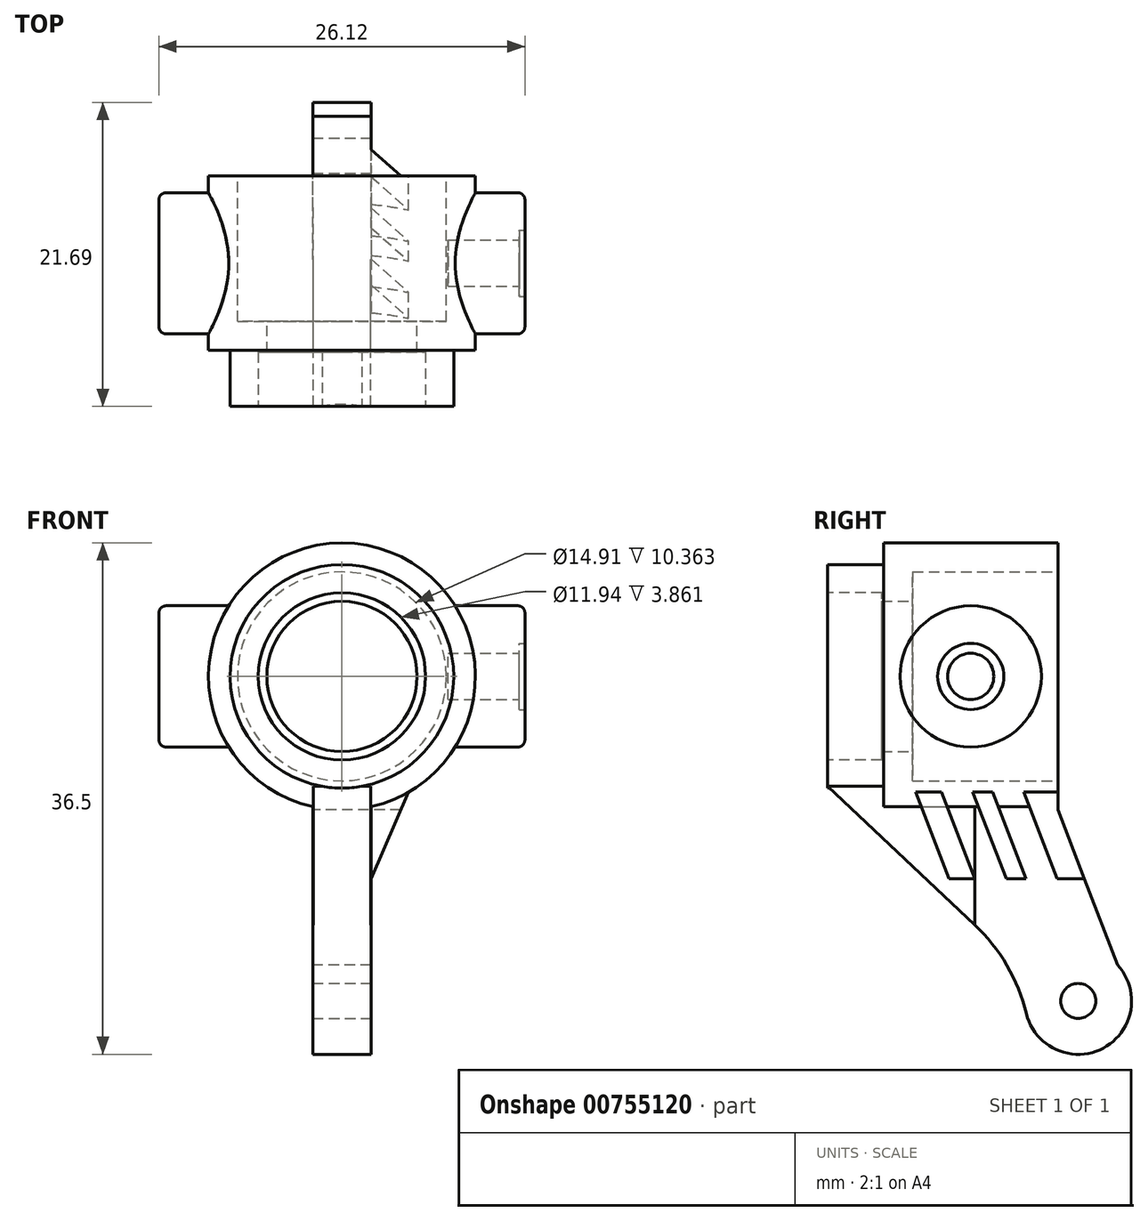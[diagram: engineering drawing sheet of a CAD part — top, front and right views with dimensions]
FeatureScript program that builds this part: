
annotation { "Feature Type Name" : "Feature", "Feature Type Description" : "" }
export const myFeature = defineFeature(function(context is Context, id is Id, definition is map)
    precondition{}
    {
        {
            var Q0;
            Q0=qCreatedBy(makeId("Front.planeOp"),FACE);
            var sketch = newSketch(context, id + "F0", { "sketchPlane" : qUnion([Q0])});
            skCircle(sketch, "E0", {"center": v(0, 0) * mm, "radius": 5.36 * mm});
            skCircle(sketch, "E1", {"center": v(0, 0) * mm, "radius": 9.53 * mm});
            skSolve(sketch);
        }
        {
            var Q0;
            Q0=makeQuery(id+"F0.imprint","IMPRINT",FACE,{"disambiguationData":[TD([[makeQuery(id+"F0.imprint","IMPRINT",EDGE,{"derivedFrom":sQuery(id+"F0.wireOp",EDGE,"E0")}),-1.0]])]});
            extrude(context, id + "F1", {"entities" : qUnion([Q0]), "depth" : 16.43 * mm, "offsetDistance" : 25.4 * mm});
        }
        {
            var Q0;
            Q0=makeQuery(id+"F1.opExtrude","CAP_FACE",FACE,{"disambiguationData":[OSD([sQuery(id+"F0.wireOp",EDGE,"E0"),sQuery(id+"F0.wireOp",EDGE,"E1")])],"isStart":true});
            var sketch = newSketch(context, id + "F2", { "sketchPlane" : qUnion([Q0])});
            skCircle(sketch, "E2", {"center": v(0, 0) * mm, "radius": 7.45 * mm});
            skSolve(sketch);
        }
        {
            var Q0;
            Q0=makeQuery(id+"F2.imprint","IMPRINT",FACE,{"disambiguationData":[TD([[makeQuery(id+"F2.imprint","IMPRINT",EDGE,{"derivedFrom":sQuery(id+"F2.wireOp",EDGE,"E2")}),1.0]])]});
            extrude(context, id + "F3", {"entities" : qUnion([Q0]), "operationType" : NewBodyOperationType.REMOVE, "oppositeDirection" : true, "depth" : 10.36 * mm, "offsetDistance" : 25.4 * mm});
        }
        {
            var Q0;
            Q0=makeQuery(id+"F1.opExtrude","CAP_FACE",FACE,{"disambiguationData":[OSD([sQuery(id+"F0.wireOp",EDGE,"E0"),sQuery(id+"F0.wireOp",EDGE,"E1")])],"isStart":false});
            var sketch = newSketch(context, id + "F4", { "sketchPlane" : qUnion([Q0])});
            skCircle(sketch, "E3", {"center": v(0, 0) * mm, "radius": 5.97 * mm});
            skSolve(sketch);
        }
        {
            var Q0;
            Q0 = qSketchRegion(id + "F4", true);
            extrude(context, id + "F5", {"entities" : qUnion([Q0]), "operationType" : NewBodyOperationType.REMOVE, "oppositeDirection" : true, "depth" : 3.86 * mm, "offsetDistance" : 25.4 * mm});
        }
        {
            var Q0;
            Q0=makeQuery(id+"F1.opExtrude","CAP_FACE",FACE,{"disambiguationData":[OSD([sQuery(id+"F0.wireOp",EDGE,"E0"),sQuery(id+"F0.wireOp",EDGE,"E1")])],"isStart":false});
            var sketch = newSketch(context, id + "F6", { "sketchPlane" : qUnion([Q0])});
            skCircle(sketch, "E4", {"center": v(0, 0) * mm, "radius": 7.98 * mm});
            skCircle(sketch, "E5.0", {"center": v(0, 0) * mm, "radius": 9.53 * mm});
            skSolve(sketch);
        }
        {
            var Q0;
            Q0 = qSketchRegion(id + "F6", true);
            extrude(context, id + "F7", {"entities" : qUnion([Q0]), "operationType" : NewBodyOperationType.REMOVE, "oppositeDirection" : true, "depth" : 4 * mm, "offsetDistance" : 25.4 * mm});
        }
        {
            var Q0;
            Q0=qCreatedBy(makeId("Right.planeOp"),FACE);
            var sketch = newSketch(context, id + "F8", { "sketchPlane" : qUnion([Q0])});
            skCircle(sketch, "E6", {"center": v(-6.22, 0) * mm, "radius": 5.04 * mm});
            skSolve(sketch);
        }
        {
            var Q0;
            Q0 = qSketchRegion(id + "F8", true);
            extrude(context, id + "F9", {"entities" : qUnion([Q0]), "operationType" : NewBodyOperationType.ADD, "endBound" : BoundingType.SYMMETRIC, "depth" : 26.1 * mm, "offsetDistance" : 25.4 * mm});
        }
        {
            var Q0;
            Q0=makeQuery(id+"F9.opExtrude","CAP_FACE",FACE,{"disambiguationData":[OSD([sQuery(id+"F8.wireOp",EDGE,"E6")])],"isStart":false});
            var sketch = newSketch(context, id + "F10", { "sketchPlane" : qUnion([Q0])});
            skPoint(sketch, "E7", {"position": v(-6.22, 0) * mm});
            skSolve(sketch);
        }
        {
            var Q0;
            Q0=qCreatedBy(makeId("Top.planeOp"),FACE);
            var sketch = newSketch(context, id + "F11", { "sketchPlane" : qUnion([Q0])});
            skLineSegment(sketch, "E8.0", {"start": v(-7.45, 0) * mm, "end": v(0, 0) * mm});
            skLineSegment(sketch, "E9", {"start": v(-7.45, -10.36) * mm, "end": v(-7.45, 0) * mm});
            skLineSegment(sketch, "E10", {"start": v(-5.97, -16.43) * mm, "end": v(-5.97, -12.57) * mm});
            skLineSegment(sketch, "E11.0", {"start": v(-4.52, -10.36) * mm, "end": v(0, -10.36) * mm, "construction": true});
            skLineSegment(sketch, "E12.0", {"start": v(0, -12.57) * mm, "end": v(-5.36, -12.57) * mm, "construction": true});
            skLineSegment(sketch, "E13", {"start": v(-5.36, -12.62) * mm, "end": v(-5.36, -10.37) * mm});
            skLineSegment(sketch, "E14", {"start": v(-5.97, -12.57) * mm, "end": v(-5.36, -12.57) * mm});
            skLineSegment(sketch, "E15", {"start": v(0, 0) * mm, "end": v(0, -16.43) * mm});
            skPoint(sketch, "E16.orphan", {"position": v(5.36, -12.57) * mm});
            skPoint(sketch, "E17.orphan", {"position": v(4.52, -10.36) * mm});
            skPoint(sketch, "E18.0.start.orphan", {"position": v(7.98, -16.43) * mm});
            skLineSegment(sketch, "E19.trimOffspring", {"start": v(0, 0) * mm, "end": v(-7.45, 0) * mm});
            skPoint(sketch, "E20.0.end.orphan", {"position": v(7.45, 0) * mm});
            skPoint(sketch, "E20.0.start.orphan", {"position": v(9.53, 0) * mm});
            skLineSegment(sketch, "E21.0", {"start": v(6.88, -10.36) * mm, "end": v(4.52, -10.36) * mm, "construction": true});
            skPoint(sketch, "E22.orphan", {"position": v(-6.88, -10.36) * mm});
            skLineSegment(sketch, "E23", {"start": v(-5.36, -10.37) * mm, "end": v(-5.36, -10.36) * mm});
            skLineSegment(sketch, "E24.trimOffspring", {"start": v(-5.36, -10.36) * mm, "end": v(-7.45, -10.36) * mm});
            skPoint(sketch, "E25.orphan", {"position": v(-7.98, -16.43) * mm});
            skLineSegment(sketch, "E26.0", {"start": v(0, -16.43) * mm, "end": v(-5.97, -16.43) * mm});
            skPoint(sketch, "E27.orphan", {"position": v(-9.53, 0) * mm});
            skSolve(sketch);
        }
        {
            var Q0;
            Q0 = qSketchRegion(id + "F11", true);
            var Q1;
            Q1=sQuery(id+"F11.wireOp",EDGE,"E15");
            revolve(context, id + "F12", {"operationType" : NewBodyOperationType.REMOVE, "surfaceOperationType" : NewSurfaceOperationType.NEW, "entities" : qUnion([Q0]), "axis" : qUnion([Q1]), "revolveType" : RevolveType.FULL, "oppositeDirection" : true});
        }
        {
            var Q0;
            Q0=qCreatedBy(makeId("Right.planeOp"),FACE);
            var sketch = newSketch(context, id + "F13", { "sketchPlane" : qUnion([Q0])});
            skLineSegment(sketch, "E28", {"start": v(-16.43, 7.98) * mm, "end": v(-12.45, 7.98) * mm});
            skLineSegment(sketch, "E29", {"start": v(-16.43, -7.85) * mm, "end": v(-5.94, -17.73) * mm});
            skLineSegment(sketch, "E30", {"start": v(-5.94, -17.73) * mm, "end": v(-5.94, -7.85) * mm});
            skLineSegment(sketch, "E31", {"start": v(-16.43, -7.85) * mm, "end": v(-5.94, -7.85) * mm});
            skSolve(sketch);
        }
        {
            var Q0;
            Q0 = qSketchRegion(id + "F13", true);
            extrude(context, id + "F14", {"entities" : qUnion([Q0]), "operationType" : NewBodyOperationType.ADD, "endBound" : BoundingType.SYMMETRIC, "depth" : 4.11 * mm, "offsetDistance" : 25.4 * mm});
        }
        {
            var Q0;
            Q0=qCreatedBy(makeId("Right.planeOp"),FACE);
            var sketch = newSketch(context, id + "F15", { "sketchPlane" : qUnion([Q0])});
            skArc(sketch, "E32", {"start": v(-2.25, -24.07) * mm, "mid": v(3.23, -26.53) * mm, "end": v(4.27, -20.6) * mm});
            skArc(sketch, "E33", {"start": v(-2.25, -24.07) * mm, "mid": v(-3.64, -20.63) * mm, "end": v(-5.94, -17.73) * mm});
            skPoint(sketch, "E34.0", {"position": v(-5.94, -17.73) * mm});
            skLineSegment(sketch, "E35.0", {"start": v(-16.43, -7.85) * mm, "end": v(-5.94, -17.73) * mm, "construction": true});
            skLineSegment(sketch, "E36", {"start": v(0, -9.52) * mm, "end": v(4.27, -20.6) * mm});
            skPoint(sketch, "E37.orphan", {"position": v(5.26, -23.16) * mm});
            skLineSegment(sketch, "E38.0", {"start": v(-5.94, -17.73) * mm, "end": v(-5.94, -9.53) * mm});
            skLineSegment(sketch, "E39", {"start": v(0, -9.53) * mm, "end": v(-5.94, -9.53) * mm, "construction": true});
            skLineSegment(sketch, "E40", {"start": v(-12.45, 9.53) * mm, "end": v(0, 9.53) * mm, "construction": true});
            skPoint(sketch, "E41.orphan", {"position": v(-5.94, -9.3) * mm});
            skLineSegment(sketch, "E42.0", {"start": v(0, -8.26) * mm, "end": v(-5.94, -8.26) * mm});
            skLineSegment(sketch, "E43", {"start": v(-5.94, -8.26) * mm, "end": v(-5.94, -9.53) * mm});
            skPoint(sketch, "E44.orphan", {"position": v(0, 9.53) * mm});
            skLineSegment(sketch, "E45.0.0", {"start": v(0, -8.26) * mm, "end": v(0, -9.53) * mm});
            skLineSegment(sketch, "E46", {"start": v(8.37, -26.97) * mm, "end": v(20.08, -26.97) * mm, "construction": true});
            skSolve(sketch);
        }
        {
            var Q0;
            Q0=makeQuery(id+"F15.imprint","IMPRINT",FACE,{"disambiguationData":[TD([[makeQuery(id+"F15.imprint","IMPRINT",EDGE,{"derivedFrom":sQuery(id+"F15.wireOp",EDGE,"E32")}),1.0]])]});
            extrude(context, id + "F16", {"entities" : qUnion([Q0]), "operationType" : NewBodyOperationType.ADD, "endBound" : BoundingType.SYMMETRIC, "depth" : 4.17 * mm, "offsetDistance" : 25.4 * mm});
        }
        {
            var Q0;
            Q0=makeQuery(id+"F16.opExtrude","CAP_FACE",FACE,{"disambiguationData":[OSD([sQuery(id+"F15.wireOp",EDGE,"E32"),sQuery(id+"F15.wireOp",EDGE,"E33"),sQuery(id+"F15.wireOp",EDGE,"E36"),sQuery(id+"F15.wireOp",EDGE,"E38.0"),sQuery(id+"F15.wireOp",EDGE,"E42.0"),sQuery(id+"F15.wireOp",EDGE,"E43"),sQuery(id+"F15.wireOp",EDGE,"E45.0.0")])],"isStart":false});
            var sketch = newSketch(context, id + "F17", { "sketchPlane" : qUnion([Q0])});
            skPoint(sketch, "E47", {"position": v(1.45, -23.16) * mm});
            skSolve(sketch);
        }
        {
            var Q0;
            Q0=sQuery(id+"F17.wireOp",VERTEX,"E47");
            var Q1;
            Q1=makeQuery(id+"F1.opExtrude","SWEPT_BODY",BODY,{"disambiguationData":[OSD([sQuery(id+"F0.wireOp",EDGE,"E0"),sQuery(id+"F0.wireOp",EDGE,"E1")])]});
            hole(context, id + "F18", {"style" : HoleStyle.SIMPLE, "endStyle" : HoleEndStyle.THROUGH, "standardTappedOrClearance" : lookupTablePath({ "fit" : "Normal", "standard" : "ISO", "engagement" : "75%", "pitch" : "0.5 mm", "size" : "2.5", "type" : "Drilled" }), "standardBlindInLast" : lookupTablePath({ "fit" : "Free", "standard" : "ISO", "engagement" : "75%", "pitch" : "0.5 mm", "size" : "2.5", "type" : "Drilled" }), "holeDiameter" : 2.5 * mm, "majorDiameter" : 3 * mm, "showTappedDepth" : true, "isTappedThrough" : true, "tappedDepth" : 12.7 * mm, "tapClearance" : 3, "locations" : qUnion([Q0]), "scope" : qUnion([Q1])});
        }
        {
            var Q0;
            Q0=makeQuery(id+"F9.opExtrude","CAP_EDGE",EDGE,{"disambiguationData":[OSD([sQuery(id+"F8.wireOp",EDGE,"E6")])],"isStart":false});
            var Q1;
            Q1=makeQuery(id+"F9.opExtrude","CAP_EDGE",EDGE,{"disambiguationData":[OSD([sQuery(id+"F8.wireOp",EDGE,"E6")])],"isStart":true});
            fillet(context, id + "F19", {"entities" : qUnion([Q0, Q1]), "radius" : 0.5 * mm, "tangentPropagation" : true, "allowEdgeOverflow" : false});
        }
        {
            var Q0;
            Q0=makeQuery(id+"F9.opExtrude","CAP_FACE",FACE,{"disambiguationData":[OSD([sQuery(id+"F8.wireOp",EDGE,"E6")])],"isStart":false});
            var sketch = newSketch(context, id + "F20", { "sketchPlane" : qUnion([Q0])});
            skCircle(sketch, "E48", {"center": v(-6.22, 0) * mm, "radius": 2.36 * mm});
            skSolve(sketch);
        }
        {
            var Q0;
            Q0 = qSketchRegion(id + "F20", true);
            extrude(context, id + "F21", {"entities" : qUnion([Q0]), "operationType" : NewBodyOperationType.REMOVE, "oppositeDirection" : true, "depth" : 0.4 * mm, "offsetDistance" : 25.4 * mm});
        }
        {
            var Q0;
            Q0=makeQuery(id+"F16.opExtrude","CAP_FACE",FACE,{"disambiguationData":[OSD([sQuery(id+"F15.wireOp",EDGE,"E32"),sQuery(id+"F15.wireOp",EDGE,"E33"),sQuery(id+"F15.wireOp",EDGE,"E36"),sQuery(id+"F15.wireOp",EDGE,"E38.0"),sQuery(id+"F15.wireOp",EDGE,"E42.0"),sQuery(id+"F15.wireOp",EDGE,"E43"),sQuery(id+"F15.wireOp",EDGE,"E45.0.0")])],"isStart":false});
            var sketch = newSketch(context, id + "F22", { "sketchPlane" : qUnion([Q0])});
            skLineSegment(sketch, "E49.0", {"start": v(0, -9.52) * mm, "end": v(1.89, -14.43) * mm});
            skLineSegment(sketch, "E50", {"start": v(1.89, -14.43) * mm, "end": v(0, -14.43) * mm});
            skLineSegment(sketch, "E51.0", {"start": v(-1.94, -9.3) * mm, "end": v(0.04, -14.43) * mm});
            skPoint(sketch, "E52.orphan", {"position": v(4.27, -20.6) * mm});
            skLineSegment(sketch, "E53.0", {"start": v(-1.94, -9.3) * mm, "end": v(0, -9.3) * mm});
            skPoint(sketch, "E54.orphan", {"position": v(-5.94, -9.3) * mm});
            skLineSegment(sketch, "E55", {"start": v(0, -9.3) * mm, "end": v(0, -9.52) * mm});
            skSolve(sketch);
        }
        {
            var Q0;
            Q0=sQuery(id+"F22.wireOp",VERTEX,"E50.start");
            var Q1;
            Q1=qCreatedBy(makeId("Front.planeOp"),FACE);
            cPlane(context, id + "F23", {"entities" : qUnion([Q0, Q1]), "cplaneType" : CPlaneType.PLANE_POINT, "offset" : 25.4 * mm, "width" : 152.4 * mm, "height" : 152.4 * mm});
        }
        {
            var Q0;
            Q0=qCreatedBy(id+"F23.planeOp",FACE);
            var sketch = newSketch(context, id + "F24", { "sketchPlane" : qUnion([Q0])});
            skLineSegment(sketch, "E56", {"start": v(0, -43.17) * mm, "end": v(101.89, -43.17) * mm});
            skPoint(sketch, "E57.0", {"position": v(2.08, -14.43) * mm});
            skLineSegment(sketch, "E58", {"start": v(2.08, -14.43) * mm, "end": v(4.76, -8.25) * mm});
            skLineSegment(sketch, "E59", {"start": v(4.76, -8.25) * mm, "end": v(4.76, -8.25) * mm});
            skLineSegment(sketch, "E60.0", {"start": v(2.08, -8.25) * mm, "end": v(2.08, -14.43) * mm});
            skLineSegment(sketch, "E61", {"start": v(4.76, -8.25) * mm, "end": v(2.08, -8.25) * mm});
            skPoint(sketch, "E62.orphan", {"position": v(2.08, -9.52) * mm});
            skSolve(sketch);
        }
        {
            var Q0;
            Q0=makeQuery(id+"F24.imprint","IMPRINT",FACE,{"disambiguationData":[TD([[makeQuery(id+"F24.imprint","IMPRINT",EDGE,{"derivedFrom":sQuery(id+"F24.wireOp",EDGE,"E58")}),1.0]])]});
            extrude(context, id + "F25", {"entities" : qUnion([Q0]), "operationType" : NewBodyOperationType.ADD, "depth" : 14.33 * mm, "offsetDistance" : 25.4 * mm});
        }
        {
            var Q0;
            {var subQ2=sQuery(id+"F22.wireOp",EDGE,"E51.0");Q0=makeQuery(id+"F22.imprint","IMPRINT",FACE,{"disambiguationData":[TD([[makeQuery(id+"F22.imprint","IMPRINT",EDGE,{"derivedFrom":subQ2}),-1.0]])]});}
            var sketch = newSketch(context, id + "F26", { "sketchPlane" : qUnion([Q0])});
            skLineSegment(sketch, "E63.0", {"start": v(0, -9.52) * mm, "end": v(1.89, -14.43) * mm});
            skLineSegment(sketch, "E64.0", {"start": v(0, -8.25) * mm, "end": v(0, -9.52) * mm});
            skLineSegment(sketch, "E65.0", {"start": v(1.89, -14.43) * mm, "end": v(1.89, -8.25) * mm});
            skLineSegment(sketch, "E66.0", {"start": v(0, -8.25) * mm, "end": v(1.89, -8.25) * mm});
            skPoint(sketch, "E67.0.end.orphan", {"position": v(0, 9.53) * mm});
            skPoint(sketch, "E67.0.start.orphan", {"position": v(0, -8.25) * mm});
            skPoint(sketch, "E68.0.end.orphan", {"position": v(4.27, -20.6) * mm});
            skSolve(sketch);
        }
        {
            var Q0;
            Q0 = qSketchRegion(id + "F26", true);
            extrude(context, id + "F27", {"entities" : qUnion([Q0]), "operationType" : NewBodyOperationType.REMOVE, "endBound" : BoundingType.SYMMETRIC, "oppositeDirection" : true, "depth" : 25.4 * mm, "offsetDistance" : 25.4 * mm});
        }
        {
            var Q0;
            Q0=makeQuery(id+"F16.opExtrude","CAP_FACE",FACE,{"disambiguationData":[OSD([sQuery(id+"F15.wireOp",EDGE,"E32"),sQuery(id+"F15.wireOp",EDGE,"E33"),sQuery(id+"F15.wireOp",EDGE,"E36"),sQuery(id+"F15.wireOp",EDGE,"E38.0"),sQuery(id+"F15.wireOp",EDGE,"E42.0"),sQuery(id+"F15.wireOp",EDGE,"E43"),sQuery(id+"F15.wireOp",EDGE,"E45.0.0")])],"isStart":false});
            var sketch = newSketch(context, id + "F28", { "sketchPlane" : qUnion([Q0])});
            skLineSegment(sketch, "E69.0", {"start": v(1.89, -14.43) * mm, "end": v(0, -9.52) * mm});
            skLineSegment(sketch, "E70.0", {"start": v(-12.44, -8.25) * mm, "end": v(0, -8.25) * mm, "construction": true});
            skLineSegment(sketch, "E71.0", {"start": v(-0.04, -14.43) * mm, "end": v(-2.42, -8.25) * mm});
            skLineSegment(sketch, "E72.0", {"start": v(-2.28, -14.43) * mm, "end": v(-4.66, -8.25) * mm});
            skLineSegment(sketch, "E73.0", {"start": v(-3.7, -14.43) * mm, "end": v(-6.07, -8.25) * mm});
            skLineSegment(sketch, "E74.0", {"start": v(-5.92, -14.43) * mm, "end": v(-8.3, -8.25) * mm});
            skLineSegment(sketch, "E75.0", {"start": v(-7.77, -14.43) * mm, "end": v(-10.16, -8.25) * mm});
            skLineSegment(sketch, "E76.0", {"start": v(-5.94, -14.43) * mm, "end": v(1.89, -14.43) * mm, "construction": true});
            skLineSegment(sketch, "E77.0", {"start": v(-12.44, -14.43) * mm, "end": v(-5.94, -14.43) * mm, "construction": true});
            skLineSegment(sketch, "E78", {"start": v(-2.28, -14.43) * mm, "end": v(-0.04, -14.43) * mm});
            skLineSegment(sketch, "E79", {"start": v(-4.66, -8.25) * mm, "end": v(-2.42, -8.25) * mm});
            skLineSegment(sketch, "E80", {"start": v(-5.92, -14.43) * mm, "end": v(-3.7, -14.43) * mm});
            skLineSegment(sketch, "E81", {"start": v(-6.07, -8.25) * mm, "end": v(-8.3, -8.25) * mm});
            skLineSegment(sketch, "E82", {"start": v(-7.77, -14.43) * mm, "end": v(-12.44, -14.43) * mm});
            skLineSegment(sketch, "E83", {"start": v(-12.44, -8.25) * mm, "end": v(-12.44, -14.43) * mm});
            skLineSegment(sketch, "E84", {"start": v(-10.16, -8.25) * mm, "end": v(-12.44, -8.25) * mm});
            skSolve(sketch);
        }
        {
            var Q0;
            Q0 = qSketchRegion(id + "F28", true);
            extrude(context, id + "F29", {"entities" : qUnion([Q0]), "operationType" : NewBodyOperationType.REMOVE, "depth" : 25.4 * mm, "offsetDistance" : 25.4 * mm});
        }
        {
            var Q0;
            Q0=makeQuery(id+"F7.boolean.opBoolean","COPY",FACE,{"derivedFrom":makeQuery(id+"F7.opExtrude","CAP_FACE",FACE,{"disambiguationData":[OSD([sQuery(id+"F6.wireOp",EDGE,"E4"),sQuery(id+"F6.wireOp",EDGE,"E5.0")])],"isStart":false})});
            var sketch = newSketch(context, id + "F30", { "sketchPlane" : qUnion([Q0])});
            skLineSegment(sketch, "E85.0", {"start": v(-4.76, -8.25) * mm, "end": v(2.08, -8.25) * mm});
            skLineSegment(sketch, "E86.0", {"start": v(4.76, -8.25) * mm, "end": v(2.08, -8.25) * mm});
            skArc(sketch, "E87.converted", {"start": v(-4.76, -8.25) * mm, "mid": v(0, -9.53) * mm, "end": v(4.76, -8.25) * mm});
            skPoint(sketch, "E88.orphan", {"position": v(-2.06, -9.3) * mm});
            skPoint(sketch, "E89.orphan", {"position": v(-2.08, -8.25) * mm});
            skSolve(sketch);
        }
        {
            var Q0;
            Q0 = qSketchRegion(id + "F30", true);
            var Q1;
            Q1=makeQuery(id+"F27.boolean.opBoolean","MERGE",FACE,{"derivedFrom":[makeQuery(id+"F16.boolean.opBoolean","MERGE",FACE,{"derivedFrom":[makeQuery(id+"F1.opExtrude","CAP_FACE",FACE,{"disambiguationData":[OSD([sQuery(id+"F0.wireOp",EDGE,"E0"),sQuery(id+"F0.wireOp",EDGE,"E1")])],"isStart":true}),makeQuery(id+"F16.opExtrude","SWEPT_FACE",FACE,{"disambiguationData":[OSD([sQuery(id+"F15.wireOp",EDGE,"E45.0.0")])]})]}),makeQuery(id+"F27.opExtrude","SWEPT_FACE",FACE,{"disambiguationData":[OSD([sQuery(id+"F26.wireOp",EDGE,"E64.0")])]})]});
            extrude(context, id + "F31", {"entities" : qUnion([Q0]), "operationType" : NewBodyOperationType.ADD, "endBound" : BoundingType.UP_TO_SURFACE, "oppositeDirection" : true, "depth" : 25.4 * mm, "endBoundEntityFace" : qUnion([Q1]), "offsetDistance" : 25.4 * mm});
        }
        {
            var Q0;
            Q0=makeQuery(id+"F10.imprint","IMPRINT",FACE,{"disambiguationData":[TD([[makeQuery(id+"F10.imprint","IMPRINT",EDGE,{"derivedFrom":makeQuery(id+"F9.opExtrude","CAP_EDGE",EDGE,{"disambiguationData":[OSD([sQuery(id+"F8.wireOp",EDGE,"E6")])],"isStart":false})}),1.0]])]});
            var sketch = newSketch(context, id + "F32", { "sketchPlane" : qUnion([Q0])});
            skCircle(sketch, "E90", {"center": v(-6.22, 0) * mm, "radius": 1.65 * mm});
            skSolve(sketch);
        }
        {
            var Q0;
            Q0 = qSketchRegion(id + "F32", true);
            extrude(context, id + "F33", {"entities" : qUnion([Q0]), "operationType" : NewBodyOperationType.REMOVE, "oppositeDirection" : true, "depth" : 5.5 * mm, "offsetDistance" : 25.4 * mm});
        }
    });
